# Revit family: Drain_Floor_Shallow_POD_PRO_Zurn-ZPD1-H
name_source: partatom
category: Plumbing Fixtures
units: mm (PartAtom-declared; Revit-internal decimal feet)

## family parameters
Always vertical = Yes
Cut with Voids When Loaded = No
Maintain Annotation Orientation = No
OmniClass Number = 23.70.50.21.24
OmniClass Title = Waste Water Drains
Part Type = Normal
Room Calculation Point = No
Round Connector Dimension = Use Radius
Shared = No
Work Plane-Based = No

## types (4) — shared parameters
Approx. Weight (Lbs) = 0' - 5 5/16"
Assembly Code = D2030300
CW Connection = No
Default Elevation = 0' - 0"
Description = Zurn POD PRO Shallow Floor Drain with Claming Frame, Floor Clamp, and Drop-in Outlet for Vinyl Sheet Flooring
HW Connection = No
Length = 0' - 6"
Main Material = Steel - Zurn - Stainless Type 304 CF8
Manufacturer = Zurn Water, LLC
Manufacurer Brand = Zurn
Model = ZPD1-H
Product Documentation Link = https://files.zurn.com
Product Installation Sheet URL = https://files.zurn.com
Product Page URL = https://www.zurn.com
Product data url = https://bimobject.com
URL = www.zurn.com
Vent Connection = No
Waste Connection = Yes
Width = 0' - 6"

## per-type parameters (varying)
| type | Outlet Outer Radius | Outlet Radius | Top Assembly | Type Comments |
| ZPD1-6H-3NH-NB | 0' - 1 3/4" | 0' - 1 1/2" | Bronze - Zurn Industrie, LLC - Polished Nickel | ZPD1-6H-3NH-NB w/ Nickel Bronze Top |
| ZPD1-6H-2NH-NB | 0' - 1 3/16" | 0' - 1" | Bronze - Zurn Industrie, LLC - Polished Nickel | ZPD1-6H-2NH-NB w/ Nickel Bronze Top |
| ZPD1-6H-3NH-SS | 0' - 1 3/4" | 0' - 1 1/2" | Steel - Zurn - Stainless Type 304 CF8 | ZPD1-6H-3NH-SS w/ Stainless Steel Top |
| ZPD1-6H-2NH-SS | 0' - 1 3/16" | 0' - 1" | Steel - Zurn - Stainless Type 304 CF8 | ZPD1-6H-2NH-SS w/ Stainless Steel Top |

## geometry (parser evidence)
native form markers: Sweep x2
no freeform markers — native parametric forms only
